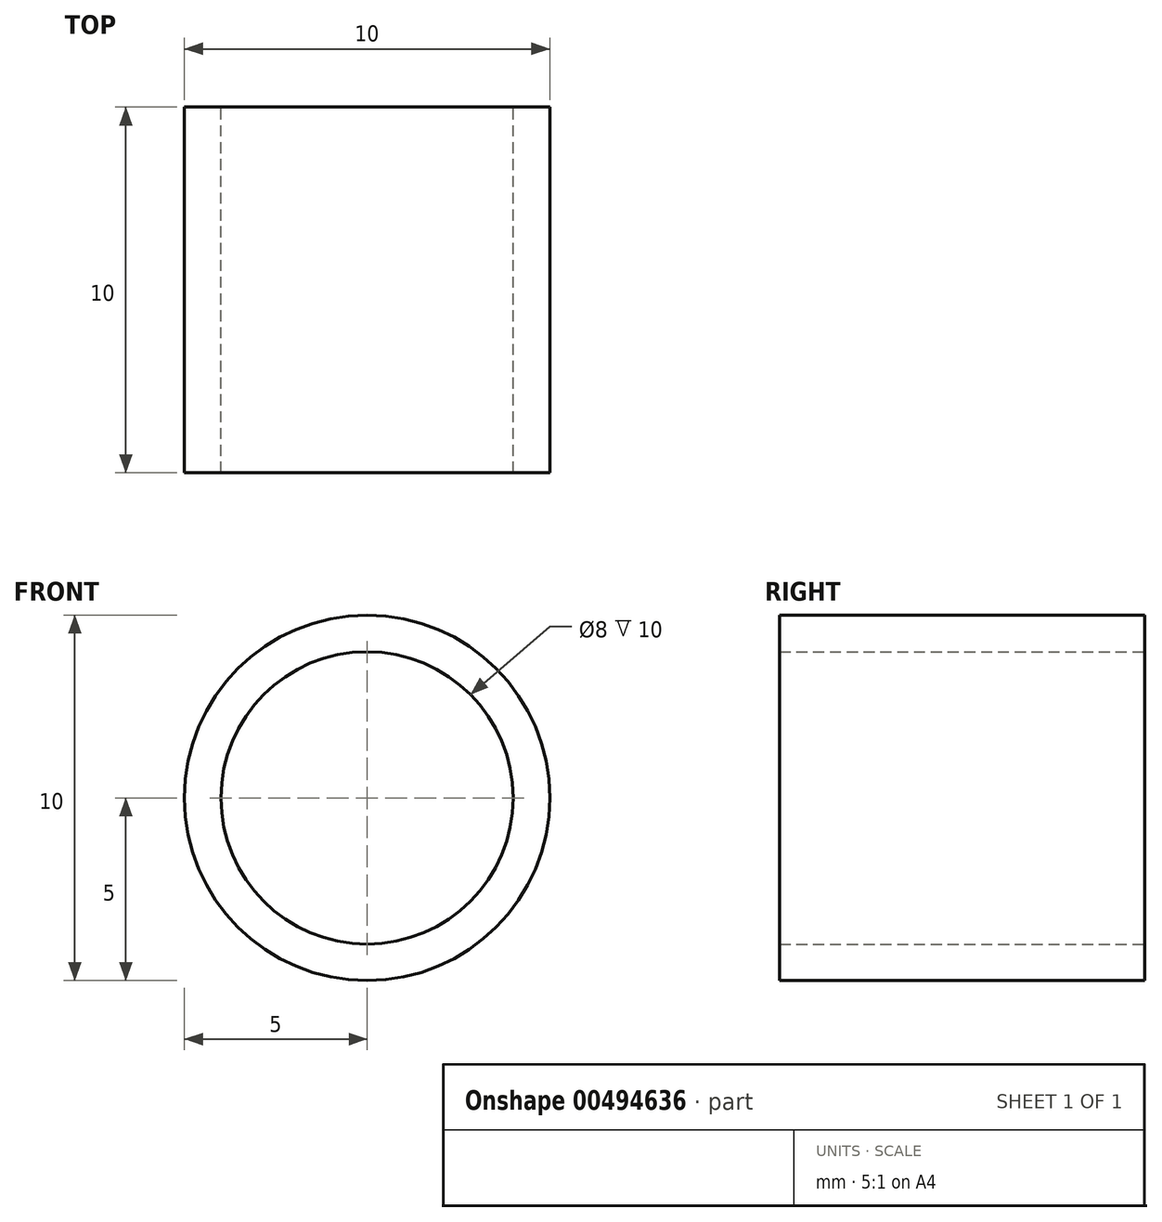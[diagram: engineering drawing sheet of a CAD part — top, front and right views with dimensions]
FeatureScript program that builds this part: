
annotation { "Feature Type Name" : "Feature", "Feature Type Description" : "" }
export const myFeature = defineFeature(function(context is Context, id is Id, definition is map)
    precondition{}
    {
        {
            var Q0;
            Q0=qCreatedBy(makeId("Front.planeOp"),FACE);
            var sketch = newSketch(context, id + "F0", { "sketchPlane" : qUnion([Q0])});
            skCircle(sketch, "E0", {"center": v(0, 0) * mm, "radius": 4 * mm});
            skCircle(sketch, "E1", {"center": v(0, 0) * mm, "radius": 5 * mm});
            skSolve(sketch);
        }
        {
            var Q0;
            Q0 = qSketchRegion(id + "F0", true);
            extrude(context, id + "F1", {"entities" : qUnion([Q0]), "depth" : 10 * mm});
        }
    });
